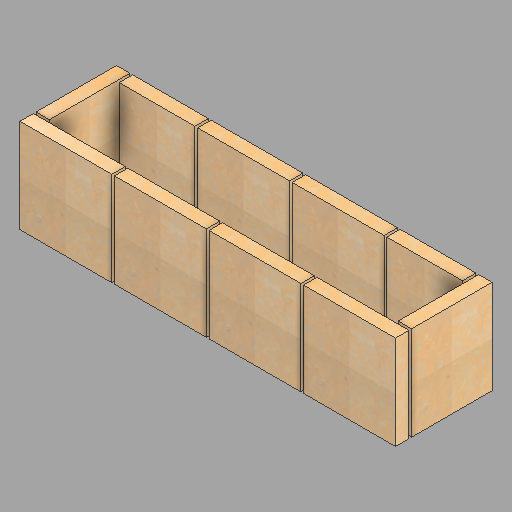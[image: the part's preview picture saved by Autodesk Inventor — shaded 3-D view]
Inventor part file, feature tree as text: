
AUTODESK INVENTOR PART (.ipt)
format: ipt  version: 2022.2 (Build 262287010, 287A)  size: 395,776 bytes
history: native  units: in
note: dims shown in document units (in); Inventor stores cm internally (conversion verified against a paired STEP export)
features: move_body x10, extrude x9, sketch x3, plane x1, mirror x1, direct_edit x1, other x1
ambient origin geometry x8: Origin, YZ Plane, XZ Plane, XY Plane, X Axis, Y Axis, Z Axis, Center Point
bodies: Solid1 (feature_tree), Solid2 (feature_tree), Solid3 (feature_tree), Solid4 (feature_tree), Solid5 (feature_tree), Solid6 (feature_tree), Solid7 (feature_tree), Solid8 (feature_tree), Solid9 (feature_tree), Solid10 (feature_tree)
feature tree (26):
  sketch  "Sketch1"  dims[d0=70.0in d1=18.0in]
  extrude  "Extrusion1"  Depth=18.0in
  extrude  "Extrusion2"  Depth=0.5in
  extrude  "Extrusion3"  Depth=0.5in
  extrude  "Extrusion4"  Depth=17.125in
  extrude  "Extrusion5"  Depth=0.5in
  plane  "Work Plane1"
  mirror  "Mirror1"
  sketch  "Sketch3"  dims[d4=17.125in d5=0.5in d6=17.125in d7=0.5in d8=17.125in d9=2.5in d10=0.0in d11=2.5in d12=0.0in d13=2.5in d14=0.0in d15=2.5in d16=0.0in d17=0.5in d19=15.0in d20=18.0in d21=2.5in d22=0.0in d23=0.5in d24=0.5in d25=2.5in d26=0.0in d27=2.5in d28=0.0in d29=2.5in d30=0.0in d31=2.5in d32=0.0in d33=0.0in d34=0.0in d35=-0.5in d36=0.0in d37=0.0in d38=-0.5in d39=0.0in d40=0.0in d41=-0.5in d42=0.0in d43=0.0in d44=-0.5in d45=0.0in d46=0.0in d47=-0.5in d48=0.0in d49=0.0in d50=-0.5in d51=0.0in d52=0.0in d53=-0.5in d54=0.0in d55=0.0in d56=-0.5in d57=0.0in d58=0.0in d59=-0.5in d60=0.0in d61=0.0in d62=-0.5in]
  extrude  "Extrusion6"  Depth=17.125in
  extrude  "Extrusion7"  Depth=2.5in TaperAngle=0.0deg
  extrude  "Extrusion8"  Depth=2.5in TaperAngle=0.0deg
  extrude  "Extrusion9"  Depth=2.5in TaperAngle=0.0deg
  direct_edit  "Direct Edit1"
  sketch  "Sketch2"  dims[d2=17.125in d3=0.5in]
  other  "Pattern of Solid5:1"
  move_body  "Move1"
  move_body  "Move2"
  move_body  "Move3"
  move_body  "Move4"
  move_body  "Move5"
  move_body  "Move6"
  move_body  "Move7"
  move_body  "Move8"
  move_body  "Move9"
  move_body  "Move10"
